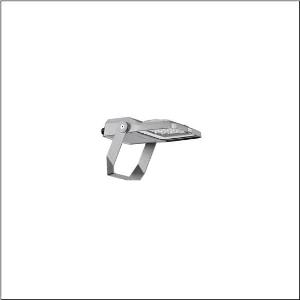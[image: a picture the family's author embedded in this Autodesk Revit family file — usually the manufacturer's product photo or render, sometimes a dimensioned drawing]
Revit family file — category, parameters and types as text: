
# Revit family: floodlight_fl_21_iq_micro___rsd12_5xa7762a4b1a_7d54
name_source: partatom
category: Lighting Fixtures
units: mm (PartAtom-declared; Revit-internal decimal feet)

## family parameters
Cut with Voids When Loaded = No
Host = Face
Light Source = No
Part Type = Normal
Room Calculation Point = No
Round Connector Dimension = Use Diameter
Shared = No

## types (1)
- --- (1 x LED, 3220 lm, 23.1 W, 4000K)
    Apparent Load = 23 VA
    CIE Flux Codes = 79 92 99 100 100
    Color Rendering = 70
    Color Temperature = 4000K
    Default Elevation = 1800 mm
    Description = Floodlight FL 21 iQ micro, floodlight, primary light control with lens, of PMMA, primary optical cover: protective disc, of toughened safety glass, transparent, light distribution: RSD12, light emission: direct distribution, installation type: surface-mounted, LED, High Power LED, rated luminous flux: 3.220lm, luminous efficacy: 139lm/W, light colour: 740, colour temperature: 4000K, control: Auto-Match, Temp-Guard, Night-Set, Smart-Wire, Desk-Remote (wireless, voltage-free reading and setting of iQ features in the workshop via application-optimized NFC function/RFID function), optimised constant luminous flux control (CLO 2.0), Street-Remote, with terminal, 6-pole, mains connection: 220..240V, AC, 50/60Hz, start of lifetime: 23W, end of service life: 24W, reduction: 11W, luminaire housing, of diecast aluminium, powder-coated, Siteco® metallic grey (DB 702S), corrosivity category C5 mid according to DIN EN ISO 12944, sealing non-destructively replaceable, mounting bracket, of steel, galvanised, powder-coated, Siteco® metallic grey (DB 702S), protection rating (complete): IP66, insulation class (complete): insulation class II (safety insulation), certification: CE, ENEC, VDE, protection symbol: D, impact resistance: IK07, permissible operating ambient temperature: -40..+40°C, permissible operating ambient temperature for outdoor applications: -40..+50°C, standard: DIN EN 12944, LABS conformity tested according to VDMA 24364:2018-05, packaging unit: 1 piece

Light Distribution: RSD12
    Height = 65 mm
    Lamp = 1 x LED
    Lamp Light Flux = 3220 lm
    Lamp Power = 23.1 W
    Lamp count = 1
    Length = 312 mm
    Luminous efficacy = 139 lm/W
    Manufacturer = Siteco
    ModVariant = No
    Model = 5XA7762A4B1A
    Mounting Place = Wall
    Mounting Type = Surface mounted
    Number of Poles = 1
    OnlyDefault = Yes
    Power Factor = 1
    Product Name = Floodlight FL 21 iQ micro | RSD12
    Product group = floodlight | wall mounted
    ProductGroupID = 2001
    Protection Class = Protection class II
    Protection Degree = IP 66
    RLX_Detail_Level = 1
    RLX_Emergency_Light_Flux = 0 lm
    RLX_Emergency_Type = 0
    RLX_Emergency_Type_DB = No
    RlxData = <blob elided: 75045 chars, md5=82f15ddb>
    Socket = socket
    Standby Power = 0 W
    System Light Flux = 3220 lm
    System Power = 23 W
    Type Comments = factory setting: luminous flux: 100 % | dim-lin: 254 | 455 mA
    Type Image = l_1006880.jpg
    URL = http://relux.com
    VarID = @adj_133233
    Voltage = 0 V
    Weight = 0.00 kg
    Width = 230 mm

## geometry (parser evidence)
native form markers: Blend x4, Sweep x12
no freeform markers — native parametric forms only
